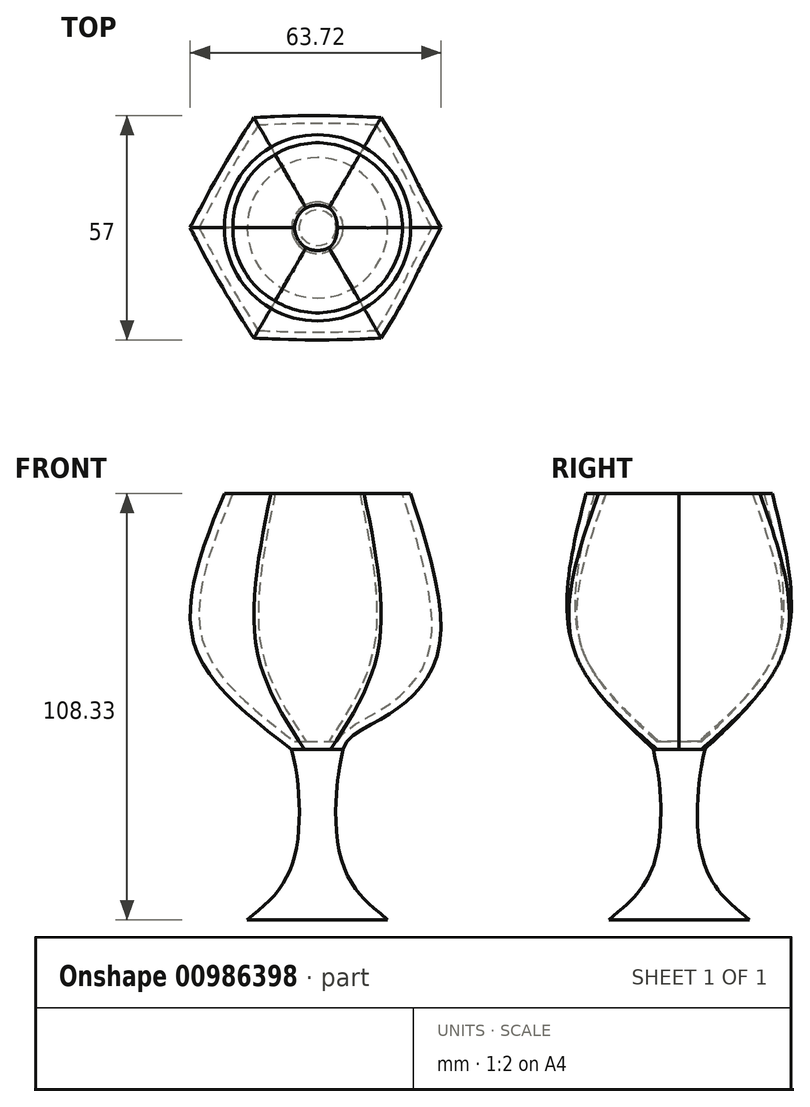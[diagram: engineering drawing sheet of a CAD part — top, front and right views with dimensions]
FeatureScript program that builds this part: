
annotation { "Feature Type Name" : "Feature", "Feature Type Description" : "" }
export const myFeature = defineFeature(function(context is Context, id is Id, definition is map)
    precondition{}
    {
        {
            var Q0;
            Q0=qCreatedBy(makeId("Front.planeOp"),FACE);
            var sketch = newSketch(context, id + "F0", { "sketchPlane" : qUnion([Q0])});
            skLineSegment(sketch, "E0", {"start": v(0, 0) * mm, "end": v(6.53, 0) * mm});
            skFitSpline(sketch, "E1", {"points": [v(6.53, 0) * mm, v(4.89, -10.01) * mm, v(5.44, -25.67) * mm, v(10.33, -36.32) * mm, v(17.85, -43.33) * mm], "startDerivative": vector(-13.97, -68.49) * mm, "endDerivative": vector(47, -40.4) * mm});
            skLineSegment(sketch, "E2", {"start": v(17.85, -43.33) * mm, "end": v(0, -43.33) * mm});
            skLineSegment(sketch, "E3", {"start": v(0, 0) * mm, "end": v(0, -43.33) * mm});
            skSolve(sketch);
        }
        {
            var Q0;
            Q0=makeQuery(id+"F0.imprint","IMPRINT",FACE,{"disambiguationData":[TD([[makeQuery(id+"F0.imprint","IMPRINT",EDGE,{"derivedFrom":sQuery(id+"F0.wireOp",EDGE,"E0")}),-1.0]])]});
            var Q1;
            Q1=sQuery(id+"F0.wireOp",EDGE,"E3");
            revolve(context, id + "F1", {"surfaceOperationType" : NewSurfaceOperationType.NEW, "entities" : qUnion([Q0]), "axis" : qUnion([Q1]), "revolveType" : RevolveType.FULL});
        }
        {
            var Q0;
            Q0=qCreatedBy(makeId("Top.planeOp"),FACE);
            var sketch = newSketch(context, id + "F2", { "sketchPlane" : qUnion([Q0])});
            skCircle(sketch, "E4.cCircle", {"center": v(0, 0) * mm, "radius": 6.53 * mm});
            skLineSegment(sketch, "E4.0", {"start": v(6.53, 0) * mm, "end": v(3.27, -5.66) * mm, "construction": true});
            skLineSegment(sketch, "E4.1", {"start": v(3.27, -5.66) * mm, "end": v(-3.27, -5.66) * mm, "construction": true});
            skLineSegment(sketch, "E4.2", {"start": v(-3.27, -5.66) * mm, "end": v(-6.53, 0) * mm, "construction": true});
            skLineSegment(sketch, "E4.3", {"start": v(-6.53, 0) * mm, "end": v(-3.27, 5.66) * mm, "construction": true});
            skLineSegment(sketch, "E4.4", {"start": v(-3.27, 5.66) * mm, "end": v(3.27, 5.66) * mm, "construction": true});
            skLineSegment(sketch, "E4.5", {"start": v(3.27, 5.66) * mm, "end": v(6.53, 0) * mm, "construction": true});
            skSolve(sketch);
        }
        {
            var Q0;
            Q0=makeQuery(id+"F2.imprint","IMPRINT",FACE,{"disambiguationData":[TD([[makeQuery(id+"F2.imprint","IMPRINT",EDGE,{"derivedFrom":sQuery(id+"F2.wireOp",EDGE,"E4.cCircle")}),1.0]])]});
            cPlane(context, id + "F3", {"entities" : qUnion([Q0]), "cplaneType" : CPlaneType.OFFSET, "offset" : 25 * mm, "width" : 150 * mm, "height" : 150 * mm});
        }
        {
            var Q0;
            Q0=qCreatedBy(id+"F3.planeOp",FACE);
            cPlane(context, id + "F4", {"entities" : qUnion([Q0]), "cplaneType" : CPlaneType.OFFSET, "offset" : 40 * mm, "width" : 150 * mm, "height" : 150 * mm});
        }
        {
            var Q0;
            Q0=qCreatedBy(id+"F3.planeOp",FACE);
            var sketch = newSketch(context, id + "F5", { "sketchPlane" : qUnion([Q0])});
            skCircle(sketch, "E5.cCircle", {"center": v(0, 0) * mm, "radius": 30.71 * mm, "construction": true});
            skLineSegment(sketch, "E5.0", {"start": v(30.71, 0) * mm, "end": v(15.36, -26.6) * mm});
            skLineSegment(sketch, "E5.1", {"start": v(15.36, -26.6) * mm, "end": v(-15.36, -26.6) * mm});
            skLineSegment(sketch, "E5.2", {"start": v(-15.36, -26.6) * mm, "end": v(-30.71, 0) * mm});
            skLineSegment(sketch, "E5.3", {"start": v(-30.71, 0) * mm, "end": v(-15.36, 26.6) * mm});
            skLineSegment(sketch, "E5.4", {"start": v(-15.36, 26.6) * mm, "end": v(15.36, 26.6) * mm});
            skLineSegment(sketch, "E5.5", {"start": v(15.36, 26.6) * mm, "end": v(30.71, 0) * mm});
            skSolve(sketch);
        }
        {
            var Q0;
            Q0=qCreatedBy(id+"F4.planeOp",FACE);
            var sketch = newSketch(context, id + "F6", { "sketchPlane" : qUnion([Q0])});
            skCircle(sketch, "E6.cCircle", {"center": v(0, 0) * mm, "radius": 23.66 * mm});
            skLineSegment(sketch, "E6.0", {"start": v(23.66, 0) * mm, "end": v(11.83, -20.5) * mm, "construction": true});
            skLineSegment(sketch, "E6.1", {"start": v(11.83, -20.5) * mm, "end": v(-11.83, -20.5) * mm, "construction": true});
            skLineSegment(sketch, "E6.2", {"start": v(-11.83, -20.5) * mm, "end": v(-23.66, 0) * mm, "construction": true});
            skLineSegment(sketch, "E6.3", {"start": v(-23.66, 0) * mm, "end": v(-11.83, 20.5) * mm, "construction": true});
            skLineSegment(sketch, "E6.4", {"start": v(-11.83, 20.5) * mm, "end": v(11.83, 20.5) * mm, "construction": true});
            skLineSegment(sketch, "E6.5", {"start": v(11.83, 20.5) * mm, "end": v(23.66, 0) * mm, "construction": true});
            skSolve(sketch);
        }
        {
            var Q0;
            Q0=qCreatedBy(makeId("Front.planeOp"),FACE);
            var sketch = newSketch(context, id + "F7", { "sketchPlane" : qUnion([Q0])});
            skFitSpline(sketch, "E7", {"points": [v(23.66, 65) * mm, v(31.34, 29.84) * mm, v(25.04, 14.52) * mm, v(14.56, 6.8) * mm, v(6.53, 0) * mm], "startDerivative": vector(27.83, -84.67) * mm, "endDerivative": vector(-9.92, -48.63) * mm});
            skSolve(sketch);
        }
        {
            var Q1;
            Q1=makeQuery(id+"F2.imprint","IMPRINT",FACE,{"disambiguationData":[TD([[makeQuery(id+"F2.imprint","IMPRINT",EDGE,{"derivedFrom":sQuery(id+"F2.wireOp",EDGE,"E4.cCircle")}),1.0]])]});
            var Q2;
            Q2=makeQuery(id+"F5.imprint","IMPRINT",FACE,{"disambiguationData":[TD([[makeQuery(id+"F5.imprint","IMPRINT",EDGE,{"derivedFrom":sQuery(id+"F5.wireOp",EDGE,"E5.0")}),-1.0]])]});
            var Q3;
            Q3=makeQuery(id+"F6.imprint","IMPRINT",FACE,{"disambiguationData":[TD([[makeQuery(id+"F6.imprint","IMPRINT",EDGE,{"derivedFrom":sQuery(id+"F6.wireOp",EDGE,"E6.cCircle")}),1.0]])]});
            var Q4;
            Q4=sQuery(id+"F7.wireOp",EDGE,"E7");
            var Q5;
            Q5=sQuery(id+"F9rhPdDJAcwSVBS_1.1.F7.wireOp",EDGE,"E7");
            var Q6;
            Q6=sQuery(id+"F9rhPdDJAcwSVBS_1.2.F7.wireOp",EDGE,"E7");
            var Q7;
            Q7=sQuery(id+"F9rhPdDJAcwSVBS_1.3.F7.wireOp",EDGE,"E7");
            var Q8;
            Q8=sQuery(id+"F9rhPdDJAcwSVBS_1.4.F7.wireOp",EDGE,"E7");
            var Q9;
            Q9=sQuery(id+"F9rhPdDJAcwSVBS_1.5.F7.wireOp",EDGE,"E7");
            var Q10;
            Q10=sQuery(id+"F2.wireOp",VERTEX,"E4.0.end");
            var Q11;
            Q11=sQuery(id+"F5.wireOp",VERTEX,"E5.0.start");
            var Q12;
            Q12=sQuery(id+"F6.wireOp",VERTEX,"E6.4.end");
            loft(context, id + "F8", {"addGuides" : true, "sheetProfilesArray" : [{ "sheetProfileEntities" : qUnion([Q1]) }, { "sheetProfileEntities" : qUnion([Q2]) }, { "sheetProfileEntities" : qUnion([Q3]) }], "guidesArray" : [{ "guideEntities" : qUnion([Q4]), "guideDerivativeType" : LoftGuideDerivativeType.DEFAULT, "guideDerivativeMagnitude" : 1 }, { "guideEntities" : qUnion([Q5]), "guideDerivativeType" : LoftGuideDerivativeType.DEFAULT, "guideDerivativeMagnitude" : 1 }, { "guideEntities" : qUnion([Q6]), "guideDerivativeType" : LoftGuideDerivativeType.DEFAULT, "guideDerivativeMagnitude" : 1 }, { "guideEntities" : qUnion([Q7]), "guideDerivativeType" : LoftGuideDerivativeType.DEFAULT, "guideDerivativeMagnitude" : 1 }, { "guideEntities" : qUnion([Q8]), "guideDerivativeType" : LoftGuideDerivativeType.DEFAULT, "guideDerivativeMagnitude" : 1 }, { "guideEntities" : qUnion([Q9]), "guideDerivativeType" : LoftGuideDerivativeType.DEFAULT, "guideDerivativeMagnitude" : 1 }], "connections" : [{ "connectionEntities" : qUnion([Q10, Q11, Q12]), "connectionEdgeQueries" : qUnion([]), "connectionEdgeParameters" : [] }]});
        }
        {
            var Q0;
            Q0=makeQuery(id+"F8.opLoft","CAP_FACE",FACE,{"disambiguationData":[OSD([makeQuery(id+"F6.imprint","IMPRINT",FACE,{"disambiguationData":[TD([[makeQuery(id+"F6.imprint","IMPRINT",EDGE,{"derivedFrom":sQuery(id+"F6.wireOp",EDGE,"E6.cCircle")}),1.0]])]})])],"isStart":true});
            shell(context, id + "F9", {"entities" : qUnion([Q0]), "thickness" : 2 * mm});
        }
    });
